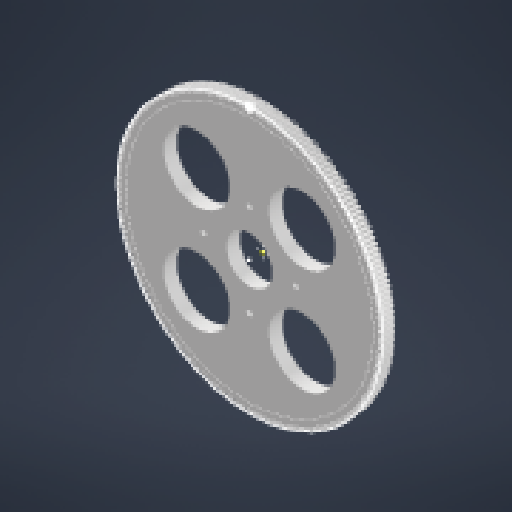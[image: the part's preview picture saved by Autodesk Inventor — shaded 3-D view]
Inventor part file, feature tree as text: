
AUTODESK INVENTOR PART (.ipt)
format: ipt  version: 2023.2 (Build 272271000, 271)  size: 868,864 bytes
history: native  units: mm
features: sketch x7, extrude x6, pattern_circular x3
ambient origin geometry x8: Origin, YZ Plane, XZ Plane, XY Plane, X Axis, Y Axis, Z Axis, Center Point
bodies: Solid1 (feature_tree)
feature tree (16):
  sketch  "Sketch1"  dims[d0=10.0mm d1=0.0mm]
  extrude  "Extrusion1"  TaperAngle=0.0deg  [1 undecoded]
  extrude  "Extrusion2"  Depth=10.0mm TaperAngle=360.0deg
  pattern_circular  "Circular Pattern1"  Count=4 Angle=360.0deg
  sketch  "Sketch4"  dims[d2=10.0mm d3=0.0mm d4=2000.0mm d5=360.0deg]
  sketch  "Sketch5"  dims[d20=35.0mm]
  extrude  "Extrusion4"  Depth=40.0mm TaperAngle=360.0deg
  extrude  "Extrusion5"  Depth=10.0mm
  pattern_circular  "Circular Pattern2"  [2 undecoded]
  extrude  "Extrusion7"  Depth=10.0mm
  pattern_circular  "Circular Pattern3"  [2 undecoded]
  extrude  "Extrusion8"  Depth=10.0mm
  sketch  "Sketch6"  dims[d21=10.0mm d22=0.0mm]
  sketch  "Sketch7"  dims[d24=10.0mm d25=0.0mm d29=40.0mm d30=360.0deg]
  sketch  "Sketch10"  dims[d42=5.0mm d43=0.0mm d44=40.0mm d45=360.0deg]
  sketch  "Sketch12"  dims[d48=7.0mm d49=4.0mm d50=10.0mm d51=10.0mm d52=10.0mm d53=10.0mm d54=10.0mm d55=10.0mm d56=0.0mm d57=0.0mm d34=1.0mm d35=1.0mm d36=1.0mm d37=0.15mm d38=0.25mm d39=0.375mm d40=14.3117mm d41=0.75mm]
note: 5 required parameter values undecoded (feature->parameter linkage not recoverable at this tier; creation-order binding heuristic only, values carry confidence <= 0.55)
